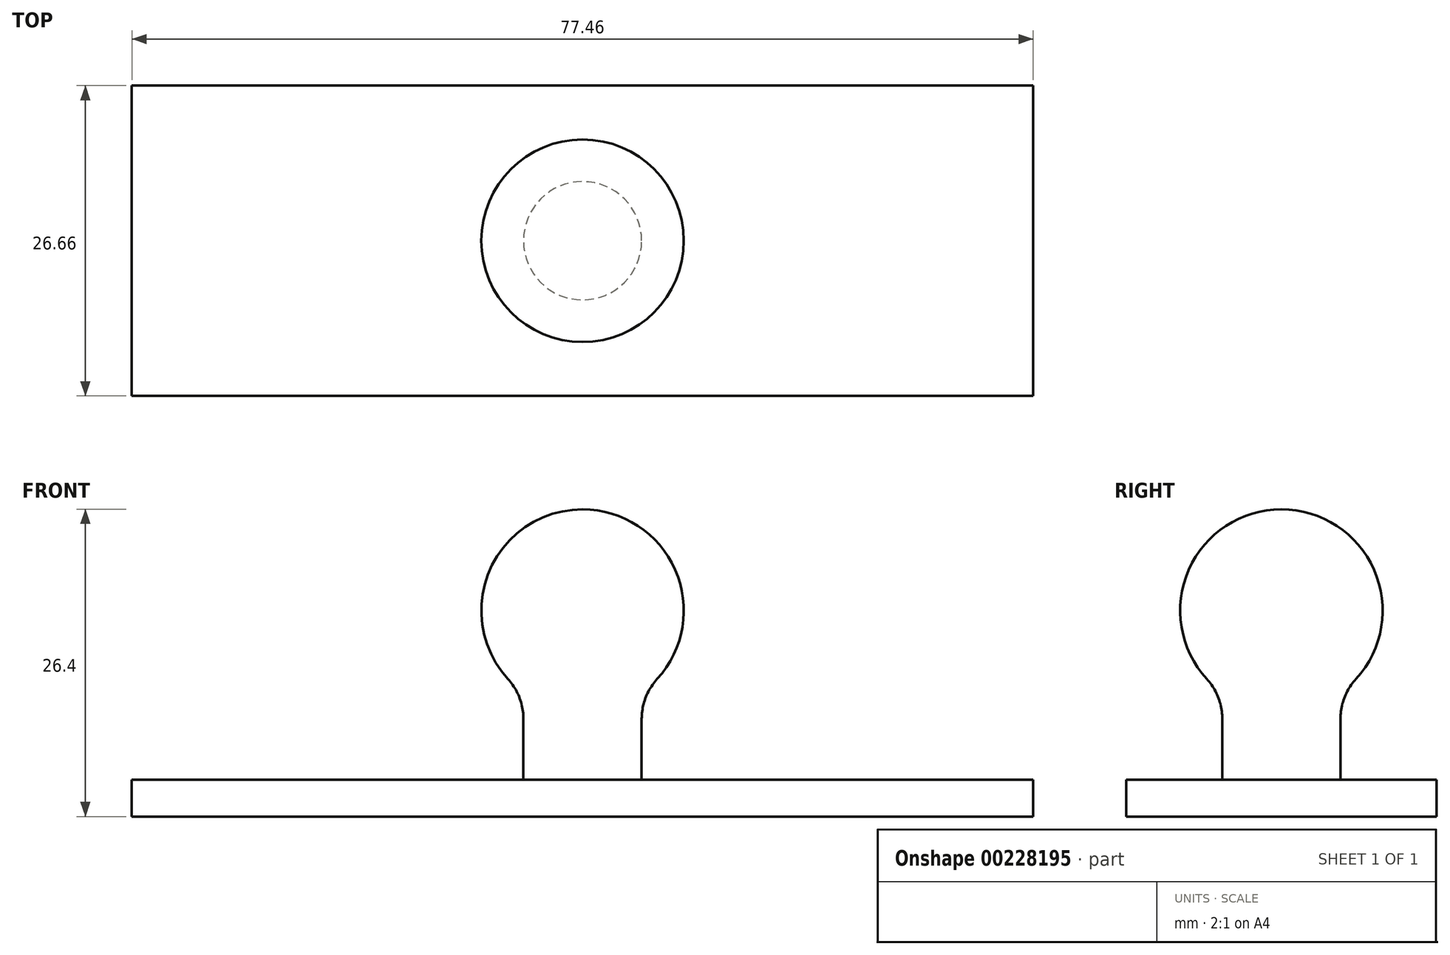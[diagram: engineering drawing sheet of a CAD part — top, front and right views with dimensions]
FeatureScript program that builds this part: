
annotation { "Feature Type Name" : "Feature", "Feature Type Description" : "" }
export const myFeature = defineFeature(function(context is Context, id is Id, definition is map)
    precondition{}
    {
        {
            var Q0;
            Q0=qCreatedBy(makeId("Top.planeOp"),FACE);
            var sketch = newSketch(context, id + "F0", { "sketchPlane" : qUnion([Q0])});
            skLineSegment(sketch, "E0.bottom", {"start": v(38.73, 13.33) * mm, "end": v(-38.73, 13.33) * mm});
            skLineSegment(sketch, "E0.top", {"start": v(38.73, -13.34) * mm, "end": v(-38.73, -13.34) * mm});
            skLineSegment(sketch, "E0.left", {"start": v(38.73, 13.33) * mm, "end": v(38.73, -13.34) * mm});
            skLineSegment(sketch, "E0.right", {"start": v(-38.73, 13.33) * mm, "end": v(-38.73, -13.34) * mm});
            skPoint(sketch, "E0.middle", {"position": v(0, 0) * mm});
            skSolve(sketch);
        }
        {
            var Q0;
            Q0 = qSketchRegion(id + "F0", true);
            extrude(context, id + "F1", {"entities" : qUnion([Q0]), "depth" : 3.17 * mm});
        }
        {
            var Q0;
            Q0=makeQuery(id+"F1.opExtrude","CAP_FACE",FACE,{"disambiguationData":[OSD([sQuery(id+"F0.wireOp",EDGE,"E0.bottom"),sQuery(id+"F0.wireOp",EDGE,"E0.top"),sQuery(id+"F0.wireOp",EDGE,"E0.left"),sQuery(id+"F0.wireOp",EDGE,"E0.right")])],"isStart":false});
            var sketch = newSketch(context, id + "F2", { "sketchPlane" : qUnion([Q0])});
            skCircle(sketch, "E1", {"center": v(0, 0) * mm, "radius": 5.08 * mm});
            skSolve(sketch);
        }
        {
            var Q0;
            Q0 = qSketchRegion(id + "F2", true);
            extrude(context, id + "F3", {"entities" : qUnion([Q0]), "operationType" : NewBodyOperationType.ADD, "depth" : 14.53 * mm});
        }
        {
            var Q0;
            Q0=qCreatedBy(makeId("Front.planeOp"),FACE);
            var sketch = newSketch(context, id + "F4", { "sketchPlane" : qUnion([Q0])});
            skLineSegment(sketch, "E2.0", {"start": v(-5.08, 17.7) * mm, "end": v(5.08, 17.7) * mm, "construction": true});
            skPoint(sketch, "E3", {"position": v(0, 17.7) * mm});
            skCircle(sketch, "E4", {"center": v(0, 17.7) * mm, "radius": 8.7 * mm, "construction": true});
            skPoint(sketch, "E5", {"position": v(0, 26.4) * mm});
            skPoint(sketch, "E6", {"position": v(0, 9) * mm});
            skPoint(sketch, "E7", {"position": v(8.7, 17.7) * mm});
            skArc(sketch, "E8", {"start": v(0, 9) * mm, "mid": v(8.7, 17.7) * mm, "end": v(0, 26.4) * mm});
            skLineSegment(sketch, "E9", {"start": v(0, 26.4) * mm, "end": v(0, 9) * mm});
            skSolve(sketch);
        }
        {
            var Q0;
            Q0 = qSketchRegion(id + "F4", true);
            var Q1;
            Q1=sQuery(id+"F4.wireOp",EDGE,"E9");
            revolve(context, id + "F5", {"operationType" : NewBodyOperationType.ADD, "entities" : qUnion([Q0]), "axis" : qUnion([Q1]), "revolveType" : RevolveType.FULL});
        }
        {
            var Q0;
            Q0=makeQuery(id+"F3.opExtrude","CAP_EDGE",EDGE,{"disambiguationData":[OSD([sQuery(id+"F2.wireOp",EDGE,"E1")])],"isStart":true});
            var Q1;
            Q1=makeQuery(id+"F5.boolean.opBoolean","INTERSECT",EDGE,{"derivedFrom":[makeQuery(id+"F3.opExtrude","SWEPT_FACE",FACE,{"disambiguationData":[OSD([sQuery(id+"F2.wireOp",EDGE,"E1")])]}),makeQuery(id+"F5.opRevolve","SWEPT_FACE",FACE,{"disambiguationData":[OSD([sQuery(id+"F4.wireOp",EDGE,"E8")])]})]});
            fillet(context, id + "F6", {"entities" : qUnion([Q0, Q1]), "radius" : 5.08 * mm, "tangentPropagation" : true, "allowEdgeOverflow" : false});
        }
    });
